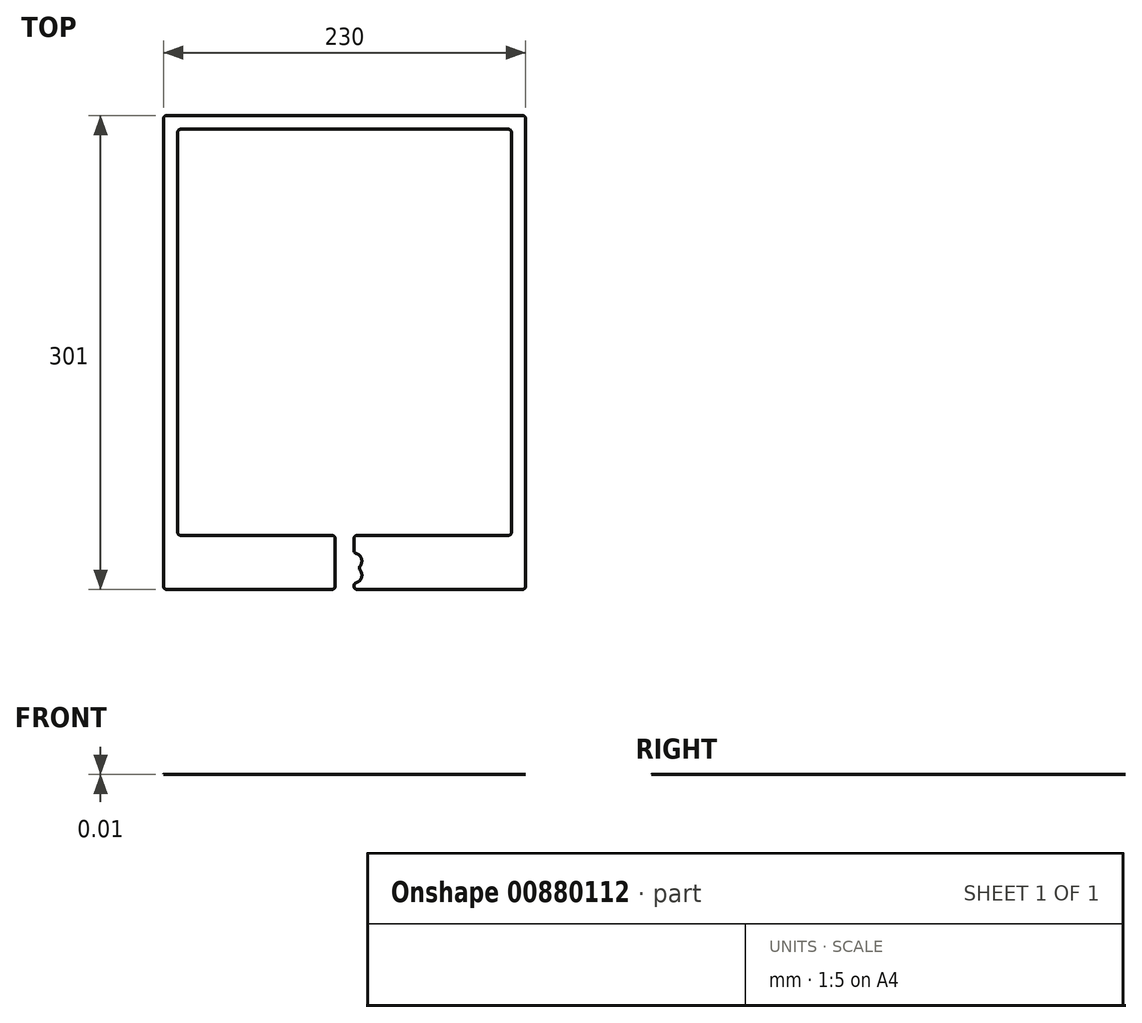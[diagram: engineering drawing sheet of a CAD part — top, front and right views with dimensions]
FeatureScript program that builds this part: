
annotation { "Feature Type Name" : "Feature", "Feature Type Description" : "" }
export const myFeature = defineFeature(function(context is Context, id is Id, definition is map)
    precondition{}
    {
        {
            var Q0;
            Q0=qCreatedBy(makeId("Top.planeOp"),FACE);
            var sketch = newSketch(context, id + "F0", { "sketchPlane" : qUnion([Q0])});
            skLineSegment(sketch, "E0.bottom", {"start": v(115, 150.5) * mm, "end": v(-115, 150.5) * mm});
            skLineSegment(sketch, "E0.top", {"start": v(115, -150.5) * mm, "end": v(6, -150.5) * mm});
            skLineSegment(sketch, "E0.left", {"start": v(115, 150.5) * mm, "end": v(115, -150.5) * mm});
            skLineSegment(sketch, "E0.right", {"start": v(-115, 150.5) * mm, "end": v(-115, -150.5) * mm});
            skLineSegment(sketch, "E1.bottom", {"start": v(102, -112.2) * mm, "end": v(-102, -112.2) * mm, "construction": true});
            skLineSegment(sketch, "E1.top", {"start": v(102, 137.8) * mm, "end": v(-102, 137.8) * mm, "construction": true});
            skLineSegment(sketch, "E1.left", {"start": v(102, -112.2) * mm, "end": v(102, 137.8) * mm, "construction": true});
            skLineSegment(sketch, "E1.right", {"start": v(-102, -112.2) * mm, "end": v(-102, 137.8) * mm, "construction": true});
            skLineSegment(sketch, "E2.0", {"start": v(106, 141.8) * mm, "end": v(-106, 141.8) * mm});
            skLineSegment(sketch, "E2.1", {"start": v(106, -116.2) * mm, "end": v(106, 141.8) * mm});
            skLineSegment(sketch, "E2.2", {"start": v(106, -116.2) * mm, "end": v(6, -116.2) * mm});
            skLineSegment(sketch, "E2.3", {"start": v(-106, -116.2) * mm, "end": v(-106, 141.8) * mm});
            skLineSegment(sketch, "E3", {"start": v(-6, -150.5) * mm, "end": v(-6, -116.2) * mm});
            skLineSegment(sketch, "E4", {"start": v(6, -116.2) * mm, "end": v(6, -127.5) * mm});
            skLineSegment(sketch, "E5", {"start": v(-6, -150.5) * mm, "end": v(-115, -150.5) * mm});
            skLineSegment(sketch, "E6", {"start": v(6, -150.5) * mm, "end": v(-6, -150.5) * mm, "construction": true});
            skLineSegment(sketch, "E7", {"start": v(6, -116.2) * mm, "end": v(-6, -116.2) * mm, "construction": true});
            skLineSegment(sketch, "E8", {"start": v(-6, -116.2) * mm, "end": v(-106, -116.2) * mm});
            skLineSegment(sketch, "E9", {"start": v(0, -116.2) * mm, "end": v(0, -150.5) * mm, "construction": true});
            skCircle(sketch, "E10", {"center": v(-3, -132.5) * mm, "radius": 1.39 * mm, "construction": true});
            skCircle(sketch, "E11", {"center": v(-3, -141.5) * mm, "radius": 1.39 * mm, "construction": true});
            skCircle(sketch, "E12.MirrorC", {"center": v(3, -132.5) * mm, "radius": 1.39 * mm, "construction": true});
            skCircle(sketch, "E13.MirrorC", {"center": v(3, -141.5) * mm, "radius": 1.39 * mm, "construction": true});
            skArc(sketch, "E14", {"start": v(6, -127.5) * mm, "mid": v(10.87, -131.38) * mm, "end": v(8.18, -137) * mm});
            skArc(sketch, "E15", {"start": v(8.18, -137) * mm, "mid": v(10.87, -142.62) * mm, "end": v(6, -146.5) * mm});
            skLineSegment(sketch, "E16.trimOffspring", {"start": v(6, -146.5) * mm, "end": v(6, -150.5) * mm});
            skSolve(sketch);
        }
        {
            var Q0;
            Q0=makeQuery(id+"F0.imprint","IMPRINT",FACE,{"disambiguationData":[TD([[makeQuery(id+"F0.imprint","IMPRINT",EDGE,{"derivedFrom":sQuery(id+"F0.wireOp",EDGE,"E0.bottom")}),1.0]])]});
            extrude(context, id + "F1", {"entities" : qUnion([Q0]), "depth" : 1 / 101.6 * mm, "offsetDistance" : 25 * mm});
        }
        {
            var Q0;
            Q0=makeQuery(id+"F1.opExtrude","SWEPT_EDGE",EDGE,{"disambiguationData":[OSD([sQuery(id+"F0.wireOp",EDGE,"E0.top"),sQuery(id+"F0.wireOp",EDGE,"E0.left")])]});
            var Q1;
            Q1=makeQuery(id+"F1.opExtrude","SWEPT_EDGE",EDGE,{"disambiguationData":[OSD([sQuery(id+"F0.wireOp",EDGE,"E0.bottom"),sQuery(id+"F0.wireOp",EDGE,"E0.left")])]});
            var Q2;
            Q2=makeQuery(id+"F1.opExtrude","SWEPT_EDGE",EDGE,{"disambiguationData":[OSD([sQuery(id+"F0.wireOp",EDGE,"E2.2"),sQuery(id+"F0.wireOp",EDGE,"E4")])]});
            var Q3;
            Q3=makeQuery(id+"F1.opExtrude","SWEPT_EDGE",EDGE,{"disambiguationData":[OSD([sQuery(id+"F0.wireOp",EDGE,"E3"),sQuery(id+"F0.wireOp",EDGE,"E8")])]});
            var Q4;
            Q4=makeQuery(id+"F1.opExtrude","SWEPT_EDGE",EDGE,{"disambiguationData":[OSD([sQuery(id+"F0.wireOp",EDGE,"E3"),sQuery(id+"F0.wireOp",EDGE,"E5")])]});
            var Q5;
            Q5=makeQuery(id+"F1.opExtrude","SWEPT_EDGE",EDGE,{"disambiguationData":[OSD([sQuery(id+"F0.wireOp",EDGE,"E2.3"),sQuery(id+"F0.wireOp",EDGE,"E8")])]});
            var Q6;
            Q6=makeQuery(id+"F1.opExtrude","SWEPT_EDGE",EDGE,{"disambiguationData":[OSD([sQuery(id+"F0.wireOp",EDGE,"E0.bottom"),sQuery(id+"F0.wireOp",EDGE,"E0.right")])]});
            var Q7;
            Q7=makeQuery(id+"F1.opExtrude","SWEPT_EDGE",EDGE,{"disambiguationData":[OSD([sQuery(id+"F0.wireOp",EDGE,"E4"),sQuery(id+"F0.wireOp",EDGE,"E14")])]});
            var Q8;
            Q8=makeQuery(id+"F1.opExtrude","SWEPT_EDGE",EDGE,{"disambiguationData":[OSD([sQuery(id+"F0.wireOp",EDGE,"E14"),sQuery(id+"F0.wireOp",EDGE,"E15")])]});
            var Q9;
            Q9=makeQuery(id+"F1.opExtrude","SWEPT_EDGE",EDGE,{"disambiguationData":[OSD([sQuery(id+"F0.wireOp",EDGE,"E15"),sQuery(id+"F0.wireOp",EDGE,"E16.trimOffspring")])]});
            var Q10;
            Q10=makeQuery(id+"F1.opExtrude","SWEPT_EDGE",EDGE,{"disambiguationData":[OSD([sQuery(id+"F0.wireOp",EDGE,"E0.right"),sQuery(id+"F0.wireOp",EDGE,"E5")])]});
            var Q11;
            Q11=makeQuery(id+"F1.opExtrude","SWEPT_EDGE",EDGE,{"disambiguationData":[OSD([sQuery(id+"F0.wireOp",EDGE,"E2.0"),sQuery(id+"F0.wireOp",EDGE,"E2.1")])]});
            var Q12;
            Q12=makeQuery(id+"F1.opExtrude","SWEPT_EDGE",EDGE,{"disambiguationData":[OSD([sQuery(id+"F0.wireOp",EDGE,"E2.1"),sQuery(id+"F0.wireOp",EDGE,"E2.2")])]});
            var Q13;
            Q13=makeQuery(id+"F1.opExtrude","SWEPT_EDGE",EDGE,{"disambiguationData":[OSD([sQuery(id+"F0.wireOp",EDGE,"E2.0"),sQuery(id+"F0.wireOp",EDGE,"E2.3")])]});
            var Q14;
            Q14=makeQuery(id+"F1.opExtrude","SWEPT_EDGE",EDGE,{"disambiguationData":[OSD([sQuery(id+"F0.wireOp",EDGE,"E0.top"),sQuery(id+"F0.wireOp",EDGE,"E16.trimOffspring")])]});
            fillet(context, id + "F2", {"entities" : qUnion([Q0, Q1, Q2, Q3, Q4, Q5, Q6, Q7, Q8, Q9, Q10, Q11, Q12, Q13, Q14]), "radius" : 2 * mm, "tangentPropagation" : true, "allowEdgeOverflow" : false});
        }
    });
